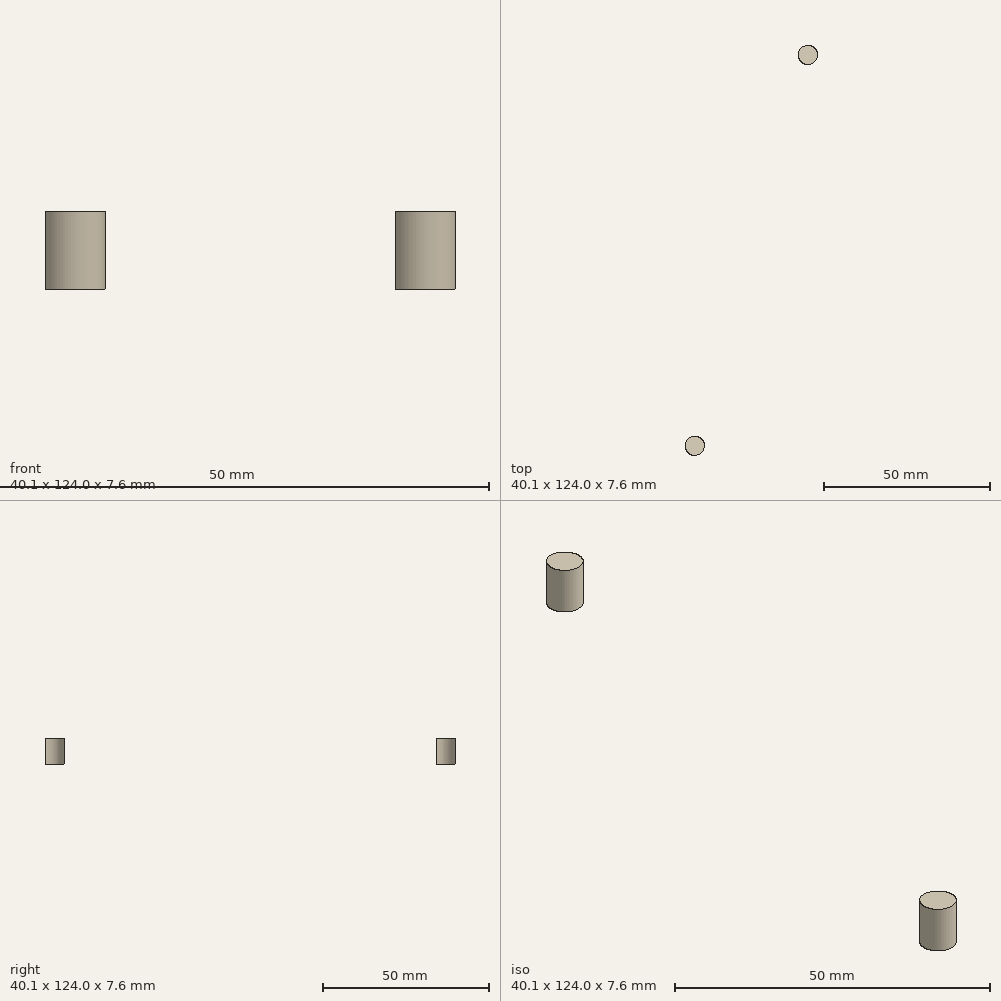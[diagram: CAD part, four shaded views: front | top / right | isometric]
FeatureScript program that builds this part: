
annotation { "Feature Type Name" : "Feature", "Feature Type Description" : "" }
export const myFeature = defineFeature(function(context is Context, id is Id, definition is map)
    precondition{}
    {
        {
            var Q0;
            Q0=qCreatedBy(makeId("Top.planeOp"),FACE);
            var sketch = newSketch(context, id + "F0", { "sketchPlane" : qUnion([Q0])});
            skLineSegment(sketch, "E0.bottom", {"start": v(-57.88, 71.17) * mm, "end": v(57.27, 71.17) * mm});
            skLineSegment(sketch, "E0.top", {"start": v(-57.88, -71.73) * mm, "end": v(57.27, -71.73) * mm});
            skLineSegment(sketch, "E0.left", {"start": v(-57.88, 71.17) * mm, "end": v(-57.88, -71.73) * mm});
            skLineSegment(sketch, "E0.right", {"start": v(57.27, 71.17) * mm, "end": v(57.27, -71.73) * mm});
            skSolve(sketch);
        }
        {
            var Q0;
            Q0=makeQuery(id+"F0.imprint","IMPRINT",FACE,{"disambiguationData":[TD([[makeQuery(id+"F0.imprint","IMPRINT",EDGE,{"derivedFrom":sQuery(id+"F0.wireOp",EDGE,"E0.bottom")}),-1.0]])]});
            extrude(context, id + "F1", {"entities" : qUnion([Q0]), "depth" : 7.62 * mm});
        }
        {
            var Q0;
            Q0=makeQuery(id+"F1.opExtrude","SWEPT_EDGE",EDGE,{"disambiguationData":[OSD([sQuery(id+"F0.wireOp",EDGE,"E0.top"),sQuery(id+"F0.wireOp",EDGE,"E0.left")])]});
            var Q1;
            Q1=makeQuery(id+"F1.opExtrude","SWEPT_EDGE",EDGE,{"disambiguationData":[OSD([sQuery(id+"F0.wireOp",EDGE,"E0.bottom"),sQuery(id+"F0.wireOp",EDGE,"E0.left")])]});
            var Q2;
            Q2=makeQuery(id+"F1.opExtrude","SWEPT_EDGE",EDGE,{"disambiguationData":[OSD([sQuery(id+"F0.wireOp",EDGE,"E0.top"),sQuery(id+"F0.wireOp",EDGE,"E0.right")])]});
            var Q3;
            Q3=makeQuery(id+"F1.opExtrude","SWEPT_EDGE",EDGE,{"disambiguationData":[OSD([sQuery(id+"F0.wireOp",EDGE,"E0.bottom"),sQuery(id+"F0.wireOp",EDGE,"E0.right")])]});
            fillet(context, id + "F2", {"entities" : qUnion([Q0, Q1, Q2, Q3]), "radius" : 5.08 * mm, "tangentPropagation" : true, "allowEdgeOverflow" : false});
        }
        {
            var Q0;
            Q0=makeQuery(id+"F1.opExtrude","CAP_FACE",FACE,{"disambiguationData":[OSD([sQuery(id+"F0.wireOp",EDGE,"E0.bottom"),sQuery(id+"F0.wireOp",EDGE,"E0.top"),sQuery(id+"F0.wireOp",EDGE,"E0.left"),sQuery(id+"F0.wireOp",EDGE,"E0.right")])],"isStart":false});
            var sketch = newSketch(context, id + "F3", { "sketchPlane" : qUnion([Q0])});
            skLineSegment(sketch, "E1", {"start": v(-53.34, 22.32) * mm, "end": v(-53.34, -21.48) * mm});
            skLineSegment(sketch, "E2", {"start": v(-48.29, -21.48) * mm, "end": v(-48.29, 22.32) * mm});
            skLineSegment(sketch, "E3", {"start": v(-48.29, 22.32) * mm, "end": v(-53.34, 22.32) * mm});
            skLineSegment(sketch, "E4", {"start": v(-53.34, -21.48) * mm, "end": v(-48.29, -21.48) * mm});
            skLineSegment(sketch, "E5.MirrorCS", {"start": v(53.34, 22.32) * mm, "end": v(53.34, -21.48) * mm});
            skLineSegment(sketch, "E6.MirrorCS", {"start": v(48.29, -21.48) * mm, "end": v(48.29, 22.32) * mm});
            skLineSegment(sketch, "E7.MirrorCS", {"start": v(53.34, -21.48) * mm, "end": v(48.29, -21.48) * mm});
            skLineSegment(sketch, "E8.MirrorCS", {"start": v(48.29, 22.32) * mm, "end": v(53.34, 22.32) * mm});
            skCircle(sketch, "E9", {"center": v(-17.13, 59.1) * mm, "radius": 2.92 * mm});
            skCircle(sketch, "E10.MirrorC", {"center": v(17.13, 59.1) * mm, "radius": 2.92 * mm});
            skCircle(sketch, "E11.MirrorC", {"center": v(17.13, -59.1) * mm, "radius": 2.92 * mm});
            skCircle(sketch, "E12.MirrorC", {"center": v(-17.13, -59.1) * mm, "radius": 2.92 * mm});
            skSolve(sketch);
        }
        {
            var Q0;
            Q0=makeQuery(id+"F3.imprint","IMPRINT",FACE,{"disambiguationData":[TD([[makeQuery(id+"F3.imprint","IMPRINT",EDGE,{"derivedFrom":sQuery(id+"F3.wireOp",EDGE,"E1")}),1.0]])]});
            var Q1;
            Q1=makeQuery(id+"F3.imprint","IMPRINT",FACE,{"disambiguationData":[TD([[makeQuery(id+"F3.imprint","IMPRINT",EDGE,{"derivedFrom":sQuery(id+"F3.wireOp",EDGE,"59KiyNNR-Zjte-ezl9-edIw-ABV5HHgXJ2Zy")}),1.0]])]});
            var Q2;
            Q2=makeQuery(id+"F3.imprint","IMPRINT",FACE,{"disambiguationData":[TD([[makeQuery(id+"F3.imprint","IMPRINT",EDGE,{"derivedFrom":sQuery(id+"F3.wireOp",EDGE,"E10.MirrorC")}),-1.0]])]});
            var Q3;
            Q3=makeQuery(id+"F3.imprint","IMPRINT",FACE,{"disambiguationData":[TD([[makeQuery(id+"F3.imprint","IMPRINT",EDGE,{"derivedFrom":sQuery(id+"F3.wireOp",EDGE,"E5.MirrorCS")}),-1.0]])]});
            var Q4;
            Q4 = qSketchRegion(id + "F0", true);
            var Q5;
            Q5=makeQuery(id+"F3.imprint","IMPRINT",FACE,{"disambiguationData":[TD([[makeQuery(id+"F3.imprint","IMPRINT",EDGE,{"derivedFrom":sQuery(id+"F3.wireOp",EDGE,"E9")}),1.0]])]});
            var Q6;
            Q6=makeQuery(id+"F3.imprint","IMPRINT",FACE,{"disambiguationData":[TD([[makeQuery(id+"F3.imprint","IMPRINT",EDGE,{"derivedFrom":sQuery(id+"F3.wireOp",EDGE,"E12.MirrorC")}),-1.0]])]});
            var Q7;
            Q7=makeQuery(id+"F3.imprint","IMPRINT",FACE,{"disambiguationData":[TD([[makeQuery(id+"F3.imprint","IMPRINT",EDGE,{"derivedFrom":sQuery(id+"F3.wireOp",EDGE,"E11.MirrorC")}),1.0]])]});
            extrude(context, id + "F4", {"entities" : qUnion([Q0, Q1, Q2, Q3, Q4, Q5, Q6, Q7]), "operationType" : NewBodyOperationType.REMOVE, "oppositeDirection" : true, "depth" : 7.62 * mm});
        }
    });
